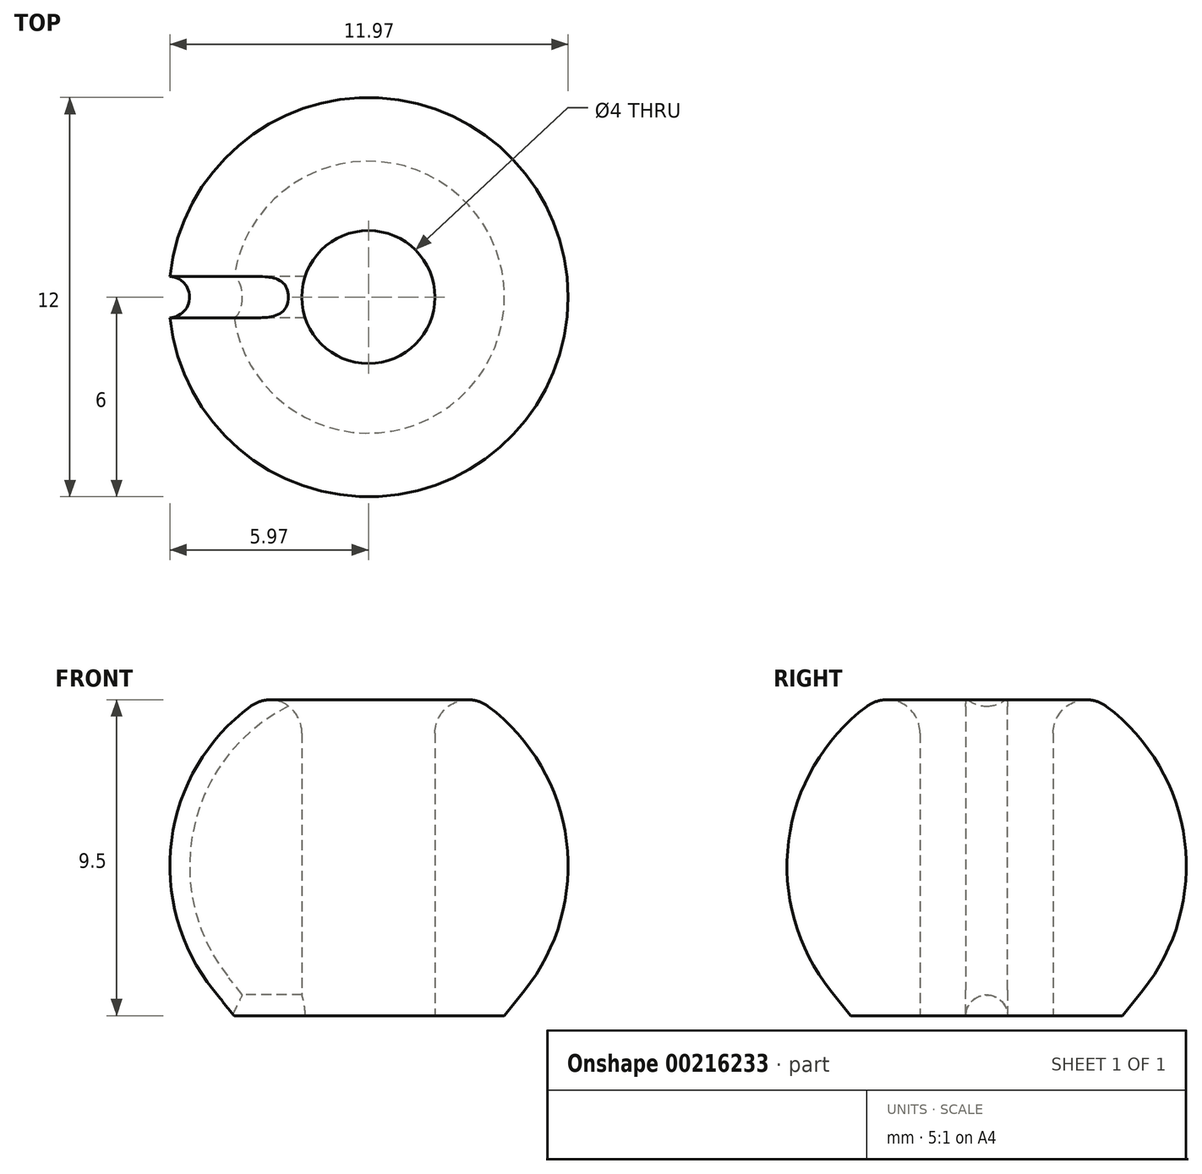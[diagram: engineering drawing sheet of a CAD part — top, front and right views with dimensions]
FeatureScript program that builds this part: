
annotation { "Feature Type Name" : "Feature", "Feature Type Description" : "" }
export const myFeature = defineFeature(function(context is Context, id is Id, definition is map)
    precondition{}
    {
        {
            var Q0;
            Q0=qCreatedBy(makeId("Front.planeOp"),FACE);
            var sketch = newSketch(context, id + "F0", { "sketchPlane" : qUnion([Q0])});
            skArc(sketch, "E0", {"start": v(0, 10.5) * mm, "mid": v(-5.4, 7.1) * mm, "end": v(-4.69, 0.75) * mm});
            skLineSegment(sketch, "E1", {"start": v(-4.09, 0) * mm, "end": v(0, 0) * mm});
            skLineSegment(sketch, "E2", {"start": v(0, 10.5) * mm, "end": v(0, 0) * mm});
            skLineSegment(sketch, "E3", {"start": v(-4.69, 0.75) * mm, "end": v(-4.09, 0) * mm});
            skPoint(sketch, "E4.orphan", {"position": v(-3.13, 0) * mm});
            skSolve(sketch);
        }
        {
            var Q0;
            Q0 = qSketchRegion(id + "F0", true);
            var Q1;
            Q1=sQuery(id+"F0.wireOp",EDGE,"E2");
            revolve(context, id + "F1", {"entities" : qUnion([Q0]), "axis" : qUnion([Q1]), "revolveType" : RevolveType.FULL});
        }
        {
            var Q0;
            Q0=makeQuery(id+"F1.opRevolve","SWEPT_FACE",FACE,{"disambiguationData":[OSD([sQuery(id+"F0.wireOp",EDGE,"E1")])]});
            var sketch = newSketch(context, id + "F2", { "sketchPlane" : qUnion([Q0])});
            skCircle(sketch, "E5", {"center": v(0, 0) * mm, "radius": 2 * mm});
            skSolve(sketch);
        }
        {
            var Q0;
            Q0 = qSketchRegion(id + "F2", true);
            extrude(context, id + "F3", {"entities" : qUnion([Q0]), "operationType" : NewBodyOperationType.REMOVE, "oppositeDirection" : true, "depth" : 25 * mm});
        }
        {
            var Q0;
            Q0=makeQuery(id+"F3.boolean.opBoolean","INTERSECT",EDGE,{"derivedFrom":[makeQuery(id+"F1.opRevolve","SWEPT_FACE",FACE,{"disambiguationData":[OSD([sQuery(id+"F0.wireOp",EDGE,"E0")])]}),makeQuery(id+"F3.opExtrude","SWEPT_FACE",FACE,{"disambiguationData":[OSD([sQuery(id+"F2.wireOp",EDGE,"E5")])]})]});
            fillet(context, id + "F4", {"entities" : qUnion([Q0]), "radius" : 1 * mm, "tangentPropagation" : true, "allowEdgeOverflow" : false});
        }
        {
            var Q0;
            Q0=qCreatedBy(makeId("Right.planeOp"),FACE);
            var sketch = newSketch(context, id + "F5", { "sketchPlane" : qUnion([Q0])});
            skCircle(sketch, "E6", {"center": v(0, 0) * mm, "radius": 0.63 * mm});
            skSolve(sketch);
        }
        {
            var Q0;
            Q0 = qSketchRegion(id + "F5", true);
            var Q1;
            Q1=sQuery(id+"F0.wireOp",EDGE,"E1");
            var Q2;
            Q2=sQuery(id+"F0.wireOp",EDGE,"E3");
            var Q3;
            Q3=sQuery(id+"F0.wireOp",EDGE,"E0");
            sweep(context, id + "F6", {"operationType" : NewBodyOperationType.REMOVE, "profiles" : qUnion([Q0]), "path" : qUnion([Q1, Q2, Q3])});
        }
    });
